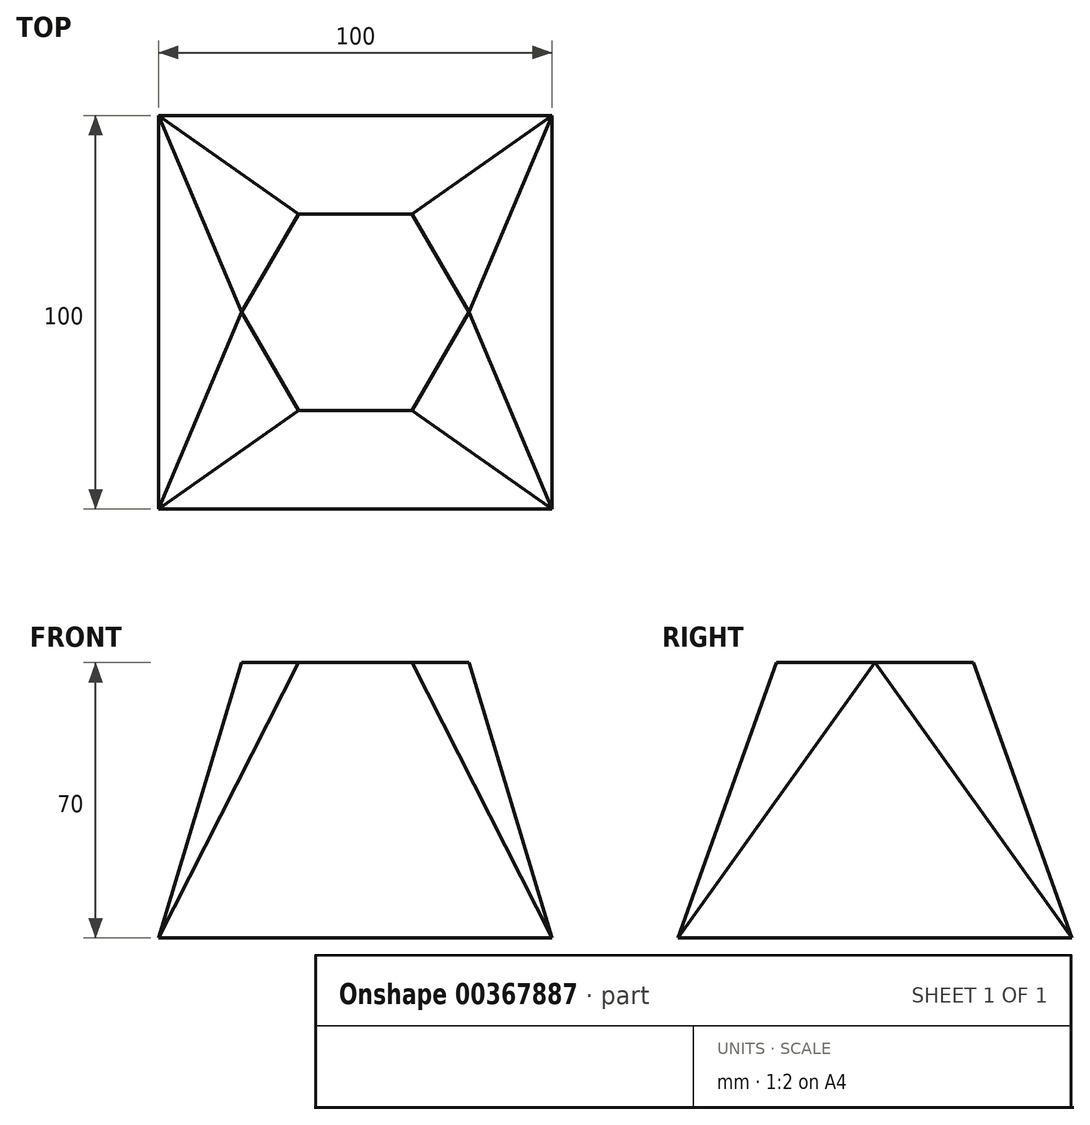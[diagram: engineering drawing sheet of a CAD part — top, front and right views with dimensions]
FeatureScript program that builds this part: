
annotation { "Feature Type Name" : "Feature", "Feature Type Description" : "" }
export const myFeature = defineFeature(function(context is Context, id is Id, definition is map)
    precondition{}
    {
        {
            var Q0;
            Q0=qCreatedBy(makeId("Top.planeOp"),FACE);
            var sketch = newSketch(context, id + "F0", { "sketchPlane" : qUnion([Q0])});
            skLineSegment(sketch, "E0.bottom", {"start": v(50, 50) * mm, "end": v(-50, 50) * mm});
            skLineSegment(sketch, "E0.top", {"start": v(50, -50) * mm, "end": v(-50, -50) * mm});
            skLineSegment(sketch, "E0.left", {"start": v(50, 50) * mm, "end": v(50, -50) * mm});
            skLineSegment(sketch, "E0.right", {"start": v(-50, 50) * mm, "end": v(-50, -50) * mm});
            skPoint(sketch, "E0.middle", {"position": v(0, 0) * mm});
            skSolve(sketch);
        }
        {
            var Q0;
            Q0=qCreatedBy(makeId("Top.planeOp"),FACE);
            cPlane(context, id + "F1", {"entities" : qUnion([Q0]), "cplaneType" : CPlaneType.OFFSET, "offset" : 70 * mm, "width" : 150 * mm, "height" : 150 * mm});
        }
        {
            var Q0;
            Q0=qCreatedBy(id+"F1.planeOp",FACE);
            var sketch = newSketch(context, id + "F2", { "sketchPlane" : qUnion([Q0])});
            skCircle(sketch, "E1.cCircle", {"center": v(0, 0) * mm, "radius": 25 * mm, "construction": true});
            skLineSegment(sketch, "E1.0", {"start": v(-14.43, 25) * mm, "end": v(14.43, 25) * mm});
            skLineSegment(sketch, "E1.1", {"start": v(14.43, 25) * mm, "end": v(28.87, 0) * mm});
            skLineSegment(sketch, "E1.2", {"start": v(28.87, 0) * mm, "end": v(14.43, -25) * mm});
            skLineSegment(sketch, "E1.3", {"start": v(14.43, -25) * mm, "end": v(-14.43, -25) * mm});
            skLineSegment(sketch, "E1.4", {"start": v(-14.43, -25) * mm, "end": v(-28.87, 0) * mm});
            skLineSegment(sketch, "E1.5", {"start": v(-28.87, 0) * mm, "end": v(-14.43, 25) * mm});
            skPoint(sketch, "E1.0.midPoint", {"position": v(0, 25) * mm});
            skLineSegment(sketch, "E2", {"start": v(-14.43, 25) * mm, "end": v(-14.43, -25) * mm});
            skLineSegment(sketch, "E3", {"start": v(14.43, 25) * mm, "end": v(14.43, -25) * mm});
            skSolve(sketch);
        }
        {
            var Q0;
            Q0=makeQuery(id+"F2.imprint","IMPRINT",FACE,{"disambiguationData":[TD([[makeQuery(id+"F2.imprint","IMPRINT",EDGE,{"derivedFrom":sQuery(id+"F2.wireOp",EDGE,"E1.0")}),-1.0]])]});
            var Q1;
            Q1=makeQuery(id+"F0.imprint","IMPRINT",FACE,{"disambiguationData":[TD([[makeQuery(id+"F0.imprint","IMPRINT",EDGE,{"derivedFrom":sQuery(id+"F0.wireOp",EDGE,"E0.bottom")}),1.0]])]});
            loft(context, id + "F3", {"sheetProfilesArray" : [{ "sheetProfileEntities" : qUnion([Q0]) }, { "sheetProfileEntities" : qUnion([Q1]) }]});
        }
        {
            var Q1;
            Q1=makeQuery(id+"F2.imprint","IMPRINT",FACE,{"disambiguationData":[TD([[makeQuery(id+"F2.imprint","IMPRINT",EDGE,{"derivedFrom":sQuery(id+"F2.wireOp",EDGE,"E1.1")}),-1.0]])]});
            var Q2;
            Q2=makeQuery(id+"F3.opLoft","MID_CAP_VERTEX",VERTEX,{"disambiguationData":[OSD([sQuery(id+"F0.wireOp",EDGE,"E0.top"),sQuery(id+"F0.wireOp",EDGE,"E0.left")])],"capPos":1.0});
            loft(context, id + "F4", {"operationType" : NewBodyOperationType.ADD, "sheetProfilesArray" : [{ "sheetProfileEntities" : qUnion([Q1]) }, { "sheetProfileEntities" : qUnion([Q2]) }]});
        }
        {
            var Q1;
            Q1=makeQuery(id+"F2.imprint","IMPRINT",FACE,{"disambiguationData":[TD([[makeQuery(id+"F2.imprint","IMPRINT",EDGE,{"derivedFrom":sQuery(id+"F2.wireOp",EDGE,"E1.1")}),-1.0]])]});
            var Q2;
            Q2=makeQuery(id+"F3.opLoft","MID_CAP_VERTEX",VERTEX,{"disambiguationData":[OSD([sQuery(id+"F0.wireOp",EDGE,"E0.bottom"),sQuery(id+"F0.wireOp",EDGE,"E0.left")])],"capPos":1.0});
            loft(context, id + "F5", {"operationType" : NewBodyOperationType.ADD, "sheetProfilesArray" : [{ "sheetProfileEntities" : qUnion([Q1]) }, { "sheetProfileEntities" : qUnion([Q2]) }]});
        }
        {
            var Q1;
            Q1=makeQuery(id+"F4.opLoft","SWEPT_FACE",FACE,{"disambiguationData":[OSD([sQuery(id+"F2.wireOp",EDGE,"E1.0"),sQuery(id+"F2.wireOp",EDGE,"E1.1"),sQuery(id+"F2.wireOp",EDGE,"E1.2"),sQuery(id+"F2.wireOp",EDGE,"E3")])]});
            var Q2;
            Q2=makeQuery(id+"F5.opLoft","SWEPT_FACE",FACE,{"disambiguationData":[OSD([sQuery(id+"F2.wireOp",EDGE,"E1.1"),sQuery(id+"F2.wireOp",EDGE,"E1.2"),sQuery(id+"F2.wireOp",EDGE,"E1.3"),sQuery(id+"F2.wireOp",EDGE,"E3")])]});
            var Q3;
            {var subQ0=sQuery(id+"F0.wireOp",EDGE,"E0.left");var subQ1=sQuery(id+"F0.wireOp",EDGE,"E0.bottom");Q3=makeQuery(id+"F5.boolean.opBoolean","MERGE",VERTEX,{"derivedFrom":[makeQuery(id+"F3.opLoft","MID_CAP_VERTEX",VERTEX,{"disambiguationData":[OSD([subQ1,subQ0])],"capPos":1.0}),makeQuery(id+"F5.opLoft","SWEPT_VERTEX",VERTEX,{"disambiguationData":[OSD([subQ1,subQ0,sQuery(id+"F2.wireOp",EDGE,"E1.1"),sQuery(id+"F2.wireOp",EDGE,"E1.2")])]})]});}
            var Q4;
            {var subQ0=sQuery(id+"F0.wireOp",EDGE,"E0.left");var subQ1=sQuery(id+"F0.wireOp",EDGE,"E0.top");Q4=makeQuery(id+"F4.boolean.opBoolean","MERGE",VERTEX,{"derivedFrom":[makeQuery(id+"F3.opLoft","MID_CAP_VERTEX",VERTEX,{"disambiguationData":[OSD([subQ1,subQ0])],"capPos":1.0}),makeQuery(id+"F4.opLoft","SWEPT_VERTEX",VERTEX,{"disambiguationData":[OSD([subQ1,subQ0,sQuery(id+"F2.wireOp",EDGE,"E1.1"),sQuery(id+"F2.wireOp",EDGE,"E1.2")])]})]});}
            loft(context, id + "F6", {"operationType" : NewBodyOperationType.ADD, "sheetProfilesArray" : [{ "sheetProfileEntities" : qUnion([Q1]) }, { "sheetProfileEntities" : qUnion([Q2]) }], "matchConnections" : true, "connections" : [{ "connectionEntities" : qUnion([Q3, Q4]), "connectionEdgeQueries" : qUnion([]), "connectionEdgeParameters" : [] }]});
        }
        {
            var Q1;
            Q1=makeQuery(id+"F2.imprint","IMPRINT",FACE,{"disambiguationData":[TD([[makeQuery(id+"F2.imprint","IMPRINT",EDGE,{"derivedFrom":sQuery(id+"F2.wireOp",EDGE,"E1.4")}),-1.0]])]});
            var Q2;
            Q2=makeQuery(id+"F3.opLoft","MID_CAP_VERTEX",VERTEX,{"disambiguationData":[OSD([sQuery(id+"F0.wireOp",EDGE,"E0.bottom"),sQuery(id+"F0.wireOp",EDGE,"E0.right")])],"capPos":1.0});
            loft(context, id + "F7", {"operationType" : NewBodyOperationType.ADD, "sheetProfilesArray" : [{ "sheetProfileEntities" : qUnion([Q1]) }, { "sheetProfileEntities" : qUnion([Q2]) }]});
        }
        {
            var Q1;
            Q1=makeQuery(id+"F2.imprint","IMPRINT",FACE,{"disambiguationData":[TD([[makeQuery(id+"F2.imprint","IMPRINT",EDGE,{"derivedFrom":sQuery(id+"F2.wireOp",EDGE,"E1.4")}),-1.0]])]});
            var Q2;
            Q2=makeQuery(id+"F3.opLoft","MID_CAP_VERTEX",VERTEX,{"disambiguationData":[OSD([sQuery(id+"F0.wireOp",EDGE,"E0.top"),sQuery(id+"F0.wireOp",EDGE,"E0.right")])],"capPos":1.0});
            loft(context, id + "F8", {"operationType" : NewBodyOperationType.ADD, "sheetProfilesArray" : [{ "sheetProfileEntities" : qUnion([Q1]) }, { "sheetProfileEntities" : qUnion([Q2]) }]});
        }
        {
            var Q1;
            Q1=makeQuery(id+"F7.opLoft","SWEPT_FACE",FACE,{"disambiguationData":[OSD([sQuery(id+"F2.wireOp",EDGE,"E1.3"),sQuery(id+"F2.wireOp",EDGE,"E1.4"),sQuery(id+"F2.wireOp",EDGE,"E1.5"),sQuery(id+"F2.wireOp",EDGE,"E2")])]});
            var Q2;
            Q2=makeQuery(id+"F8.opLoft","SWEPT_FACE",FACE,{"disambiguationData":[OSD([sQuery(id+"F2.wireOp",EDGE,"E1.0"),sQuery(id+"F2.wireOp",EDGE,"E1.4"),sQuery(id+"F2.wireOp",EDGE,"E1.5"),sQuery(id+"F2.wireOp",EDGE,"E2")])]});
            var Q3;
            {var subQ0=sQuery(id+"F0.wireOp",EDGE,"E0.right");var subQ1=sQuery(id+"F0.wireOp",EDGE,"E0.top");Q3=makeQuery(id+"F8.boolean.opBoolean","MERGE",VERTEX,{"derivedFrom":[makeQuery(id+"F3.opLoft","MID_CAP_VERTEX",VERTEX,{"disambiguationData":[OSD([subQ1,subQ0])],"capPos":1.0}),makeQuery(id+"F8.opLoft","SWEPT_VERTEX",VERTEX,{"disambiguationData":[OSD([subQ1,subQ0,sQuery(id+"F2.wireOp",EDGE,"E1.3"),sQuery(id+"F2.wireOp",EDGE,"E1.4"),sQuery(id+"F2.wireOp",EDGE,"E2")])]})]});}
            var Q4;
            {var subQ0=sQuery(id+"F0.wireOp",EDGE,"E0.right");var subQ1=sQuery(id+"F0.wireOp",EDGE,"E0.bottom");Q4=makeQuery(id+"F7.boolean.opBoolean","MERGE",VERTEX,{"derivedFrom":[makeQuery(id+"F3.opLoft","MID_CAP_VERTEX",VERTEX,{"disambiguationData":[OSD([subQ1,subQ0])],"capPos":1.0}),makeQuery(id+"F7.opLoft","SWEPT_VERTEX",VERTEX,{"disambiguationData":[OSD([subQ1,subQ0,sQuery(id+"F2.wireOp",EDGE,"E1.3"),sQuery(id+"F2.wireOp",EDGE,"E1.4"),sQuery(id+"F2.wireOp",EDGE,"E2")])]})]});}
            loft(context, id + "F9", {"operationType" : NewBodyOperationType.ADD, "sheetProfilesArray" : [{ "sheetProfileEntities" : qUnion([Q1]) }, { "sheetProfileEntities" : qUnion([Q2]) }], "matchConnections" : true, "connections" : [{ "connectionEntities" : qUnion([Q3, Q4]), "connectionEdgeQueries" : qUnion([]), "connectionEdgeParameters" : [] }]});
        }
    });
